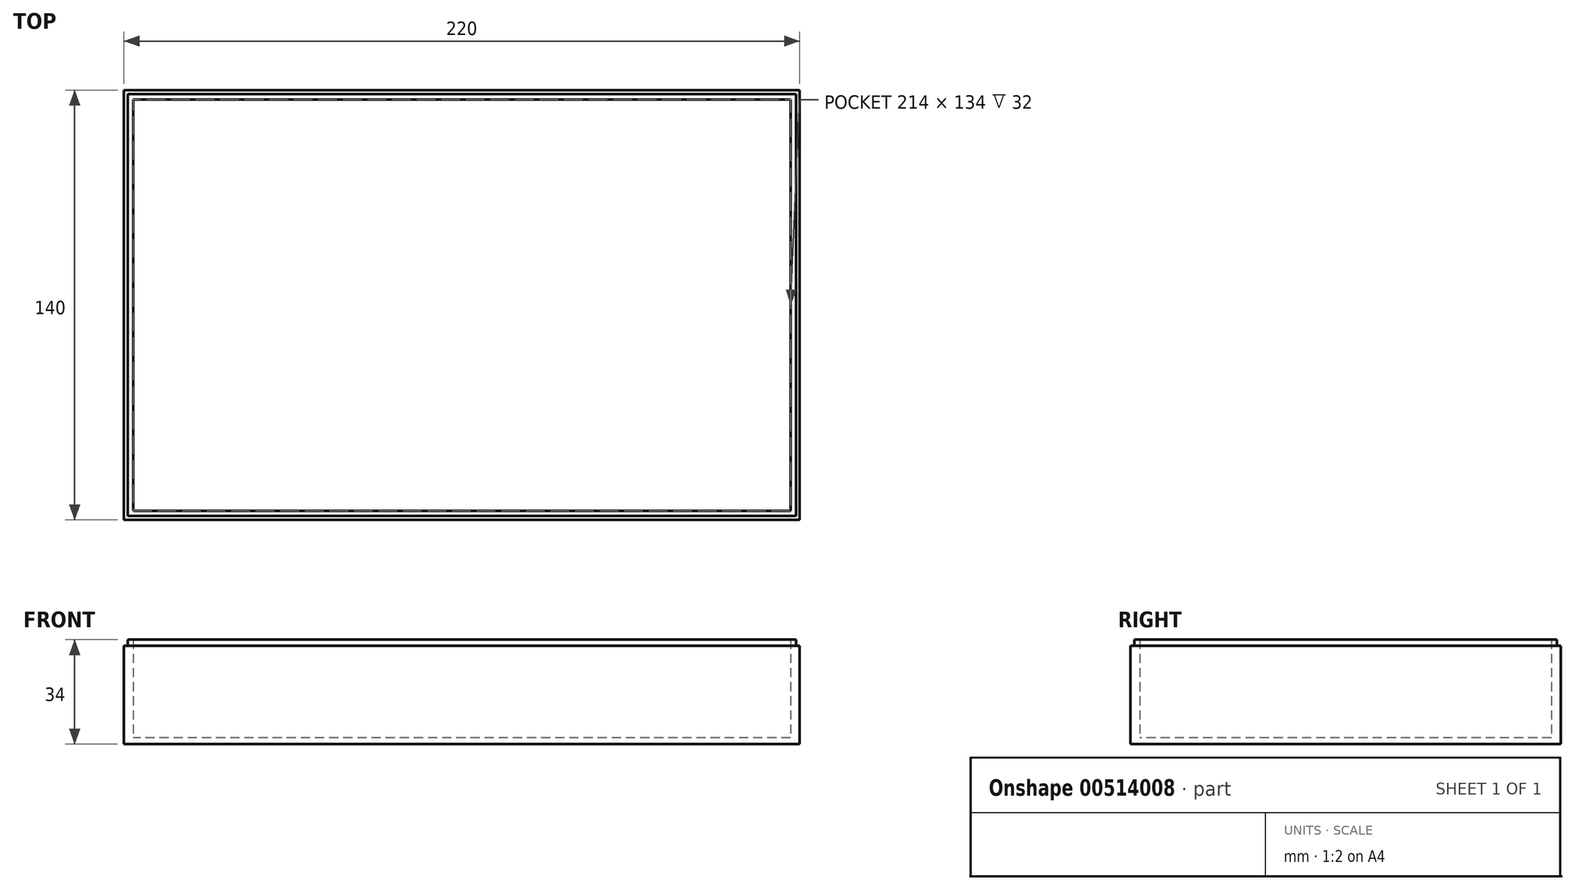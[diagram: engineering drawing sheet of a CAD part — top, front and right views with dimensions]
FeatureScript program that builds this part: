
annotation { "Feature Type Name" : "Feature", "Feature Type Description" : "" }
export const myFeature = defineFeature(function(context is Context, id is Id, definition is map)
    precondition{}
    {
        {
            var Q0;
            Q0=qCreatedBy(makeId("Top.planeOp"),FACE);
            var sketch = newSketch(context, id + "F0", { "sketchPlane" : qUnion([Q0])});
            skLineSegment(sketch, "E0.bottom", {"start": v(110, 70) * mm, "end": v(-110, 70) * mm});
            skLineSegment(sketch, "E0.top", {"start": v(110, -70) * mm, "end": v(-110, -70) * mm});
            skLineSegment(sketch, "E0.left", {"start": v(110, 70) * mm, "end": v(110, -70) * mm});
            skLineSegment(sketch, "E0.right", {"start": v(-110, 70) * mm, "end": v(-110, -70) * mm});
            skPoint(sketch, "E0.middle", {"position": v(0, 0) * mm});
            skSolve(sketch);
        }
        {
            var Q0;
            Q0=makeQuery(id+"F0.imprint","IMPRINT",FACE,{"disambiguationData":[TD([[makeQuery(id+"F0.imprint","IMPRINT",EDGE,{"derivedFrom":sQuery(id+"F0.wireOp",EDGE,"E0.bottom")}),1.0]])]});
            extrude(context, id + "F1", {"entities" : qUnion([Q0]), "depth" : 2 * mm});
        }
        {
            var Q0;
            Q0=makeQuery(id+"F1.opExtrude","CAP_FACE",FACE,{"disambiguationData":[OSD([sQuery(id+"F0.wireOp",EDGE,"E0.bottom"),sQuery(id+"F0.wireOp",EDGE,"E0.top"),sQuery(id+"F0.wireOp",EDGE,"E0.left"),sQuery(id+"F0.wireOp",EDGE,"E0.right")])],"isStart":false});
            var sketch = newSketch(context, id + "F2", { "sketchPlane" : qUnion([Q0])});
            skLineSegment(sketch, "E1.bottom", {"start": v(107, 67) * mm, "end": v(-107, 67) * mm});
            skLineSegment(sketch, "E1.top", {"start": v(107, -67) * mm, "end": v(-107, -67) * mm});
            skLineSegment(sketch, "E1.left", {"start": v(107, 67) * mm, "end": v(107, -67) * mm});
            skLineSegment(sketch, "E1.right", {"start": v(-107, 67) * mm, "end": v(-107, -67) * mm});
            skPoint(sketch, "E1.middle", {"position": v(0, 0) * mm});
            skSolve(sketch);
        }
        {
            var Q0;
            Q0=makeQuery(id+"F2.imprint","IMPRINT",FACE,{"disambiguationData":[TD([[makeQuery(id+"F2.imprint","IMPRINT",EDGE,{"derivedFrom":sQuery(id+"F2.wireOp",EDGE,"E1.bottom")}),-1.0]])]});
            extrude(context, id + "F3", {"entities" : qUnion([Q0]), "operationType" : NewBodyOperationType.ADD, "depth" : 30 * mm});
        }
        {
            var Q0;
            Q0=makeQuery(id+"F3.opExtrude","CAP_FACE",FACE,{"disambiguationData":[OSD([sQuery(id+"F0.wireOp",EDGE,"E0.bottom"),sQuery(id+"F0.wireOp",EDGE,"E0.top"),sQuery(id+"F0.wireOp",EDGE,"E0.left"),sQuery(id+"F0.wireOp",EDGE,"E0.right"),sQuery(id+"F2.wireOp",EDGE,"E1.bottom"),sQuery(id+"F2.wireOp",EDGE,"E1.top"),sQuery(id+"F2.wireOp",EDGE,"E1.left"),sQuery(id+"F2.wireOp",EDGE,"E1.right")])],"isStart":false});
            var sketch = newSketch(context, id + "F4", { "sketchPlane" : qUnion([Q0])});
            skLineSegment(sketch, "E2.bottom", {"start": v(108.75, 68.75) * mm, "end": v(-108.75, 68.75) * mm});
            skLineSegment(sketch, "E2.top", {"start": v(108.75, -68.75) * mm, "end": v(-108.75, -68.75) * mm});
            skLineSegment(sketch, "E2.left", {"start": v(108.75, 68.75) * mm, "end": v(108.75, -68.75) * mm});
            skLineSegment(sketch, "E2.right", {"start": v(-108.75, 68.75) * mm, "end": v(-108.75, -68.75) * mm});
            skPoint(sketch, "E2.middle", {"position": v(0, 0) * mm});
            skSolve(sketch);
        }
        {
            var Q0;
            Q0=makeQuery(id+"F4.imprint","IMPRINT",FACE,{"disambiguationData":[TD([[makeQuery(id+"F4.imprint","IMPRINT",EDGE,{"derivedFrom":sQuery(id+"F4.wireOp",EDGE,"E2.bottom")}),1.0]])]});
            extrude(context, id + "F5", {"entities" : qUnion([Q0]), "operationType" : NewBodyOperationType.ADD, "depth" : 2 * mm});
        }
    });
